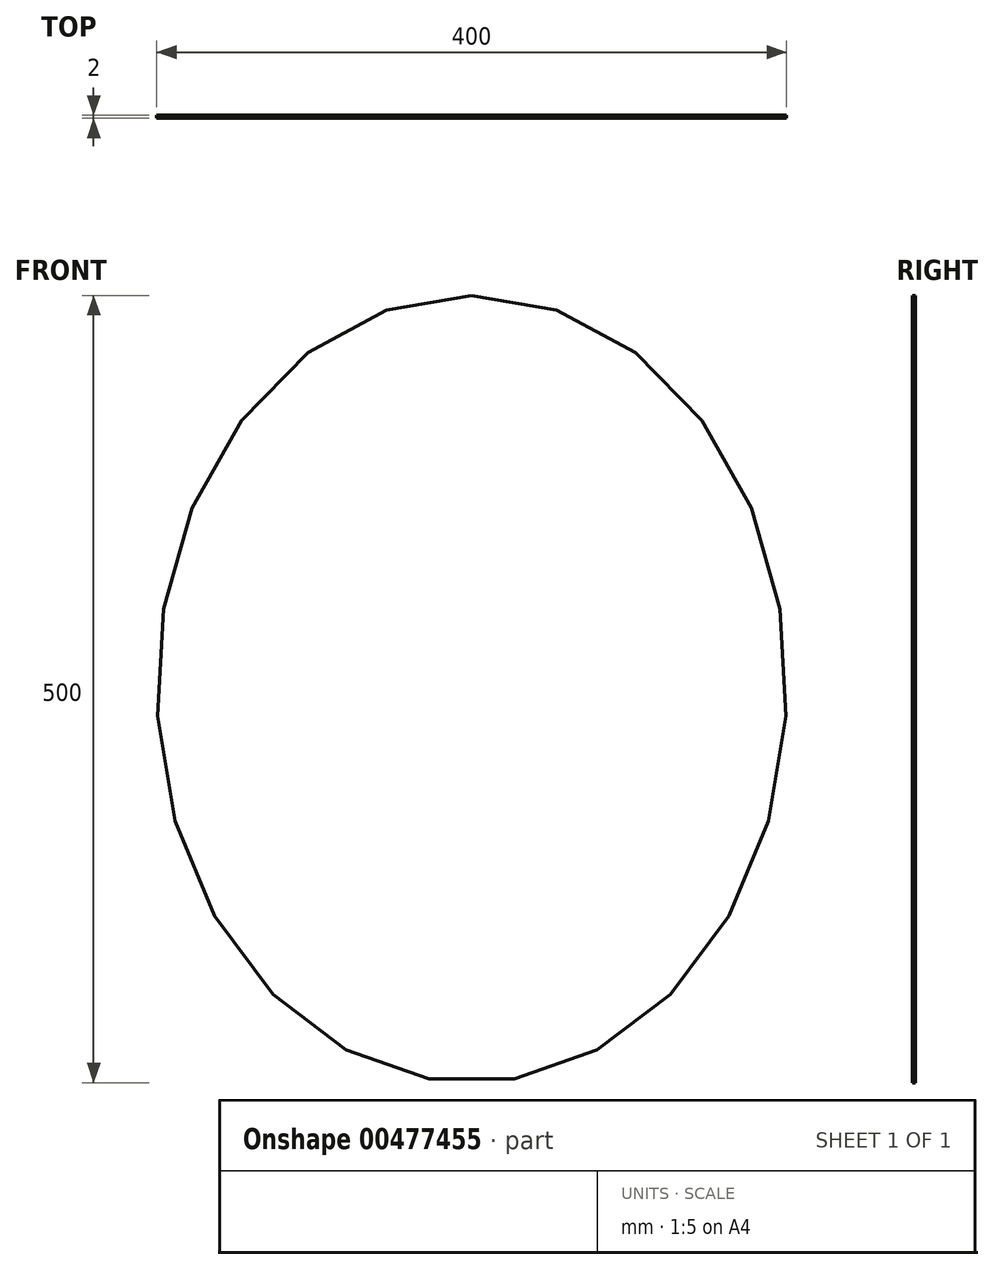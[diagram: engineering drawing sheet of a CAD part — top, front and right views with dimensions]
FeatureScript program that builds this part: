
annotation { "Feature Type Name" : "Feature", "Feature Type Description" : "" }
export const myFeature = defineFeature(function(context is Context, id is Id, definition is map)
    precondition{}
    {
        {
            var Q0;
            Q0=qCreatedBy(makeId("Front.planeOp"),FACE);
            var sketch = newSketch(context, id + "F0", { "sketchPlane" : qUnion([Q0])});
            skEllipse(sketch, "E0", {"center": v(0, 0) * mm, "majorRadius": 250 * mm, "minorRadius": 200 * mm, "majorAxis": v(0, 1)});
            skSolve(sketch);
        }
        {
            var Q0;
            Q0=makeQuery(id+"F0.imprint","IMPRINT",FACE,{"disambiguationData":[TD([[makeQuery(id+"F0.imprint","IMPRINT",EDGE,{"derivedFrom":sQuery(id+"F0.wireOp",EDGE,"E0")}),1.0]])]});
            extrude(context, id + "F1", {"entities" : qUnion([Q0]), "depth" : 2 * mm});
        }
    });
